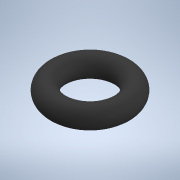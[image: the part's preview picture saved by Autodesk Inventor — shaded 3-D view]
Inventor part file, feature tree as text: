
AUTODESK INVENTOR PART (.ipt)
format: ipt  version: 2020.3 (Build 243373000, 373)  size: 144,384 bytes
history: native  units: mm
features: revolve x1, sketch x1
ambient origin geometry x8: Origin, YZ Plane, XZ Plane, XY Plane, X Axis, Y Axis, Z Axis, Center Point
bodies: Solid1 (feature_tree)
feature tree (2):
  revolve  "Revolution1"  [1 undecoded]
  sketch  "Sketch1"  dims[d0=1.78mm d1=2.73mm d2=90.0deg]
note: 1 required parameter value undecoded (feature->parameter linkage not recoverable at this tier; creation-order binding heuristic only, values carry confidence <= 0.55)
